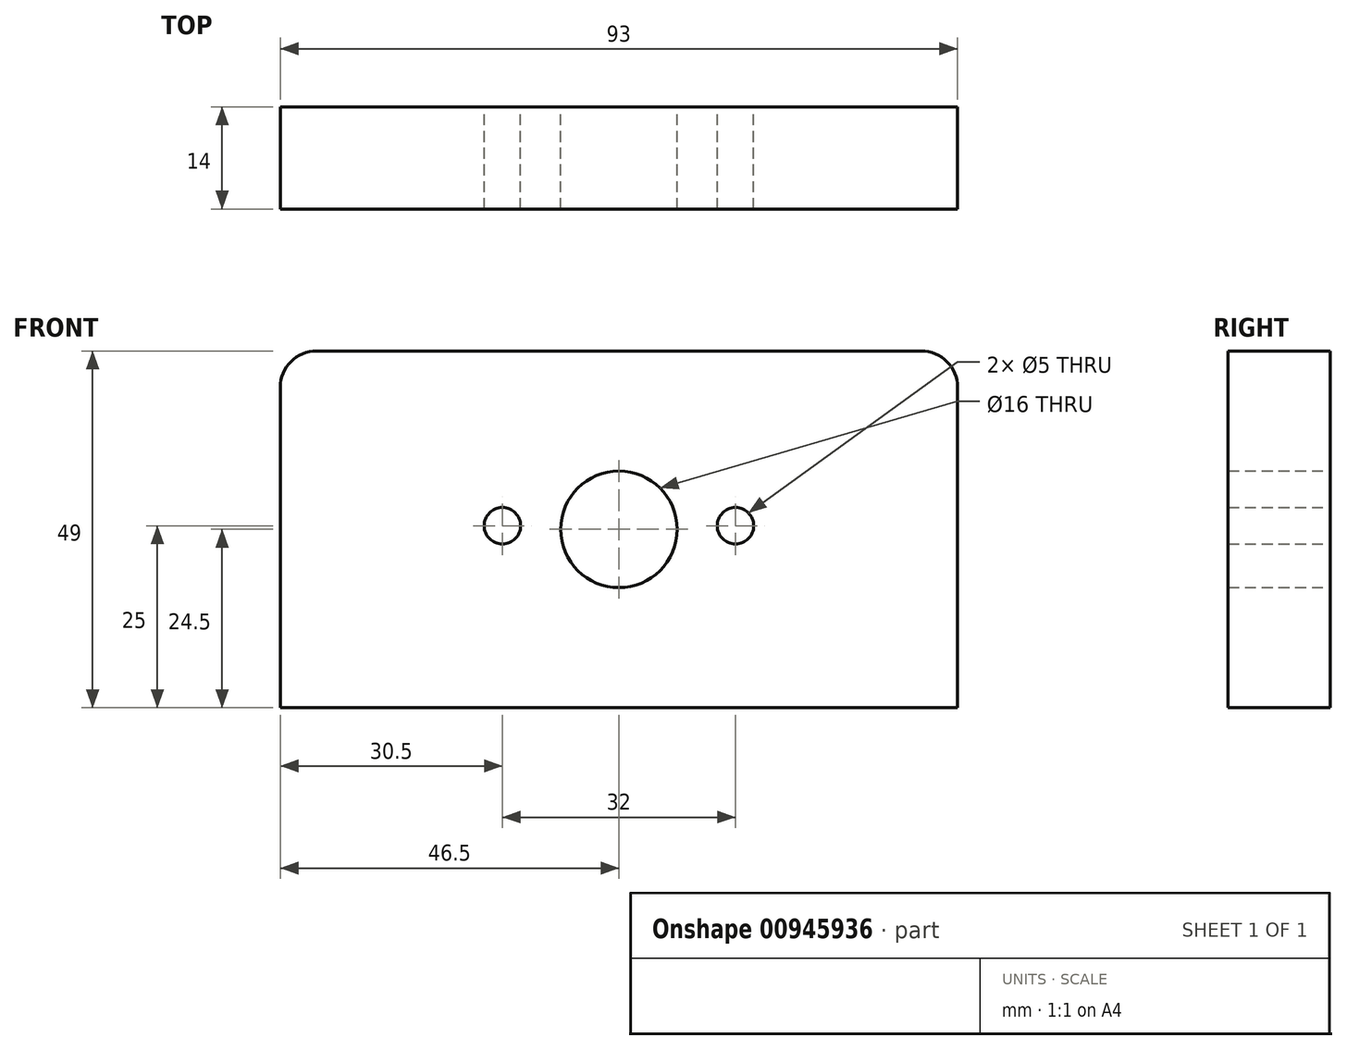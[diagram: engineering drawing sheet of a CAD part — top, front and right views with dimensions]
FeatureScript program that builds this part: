
annotation { "Feature Type Name" : "Feature", "Feature Type Description" : "" }
export const myFeature = defineFeature(function(context is Context, id is Id, definition is map)
    precondition{}
    {
        {
            var Q0;
            Q0=qCreatedBy(makeId("Front.planeOp"),FACE);
            var sketch = newSketch(context, id + "F0", { "sketchPlane" : qUnion([Q0])});
            skLineSegment(sketch, "E0.bottom", {"start": v(46.5, -24.5) * mm, "end": v(-46.5, -24.5) * mm});
            skLineSegment(sketch, "E0.top", {"start": v(41.5, 24.5) * mm, "end": v(-41.5, 24.5) * mm});
            skLineSegment(sketch, "E0.left", {"start": v(46.5, -24.5) * mm, "end": v(46.5, 19.5) * mm});
            skLineSegment(sketch, "E0.right", {"start": v(-46.5, -24.5) * mm, "end": v(-46.5, 19.5) * mm});
            skPoint(sketch, "E0.middle", {"position": v(0, 0) * mm});
            skPoint(sketch, "E1.visualSharp", {"position": v(-46.5, 24.5) * mm});
            skArc(sketch, "E1.filletArc", {"start": v(-41.5, 24.5) * mm, "mid": v(-45.04, 23.04) * mm, "end": v(-46.5, 19.5) * mm});
            skPoint(sketch, "E2.visualSharp", {"position": v(46.5, 24.5) * mm});
            skArc(sketch, "E2.filletArc", {"start": v(46.5, 19.5) * mm, "mid": v(45.04, 23.04) * mm, "end": v(41.5, 24.5) * mm});
            skCircle(sketch, "E3", {"center": v(0, 0) * mm, "radius": 8 * mm});
            skCircle(sketch, "E4", {"center": v(-16, 0.5) * mm, "radius": 2.5 * mm});
            skLineSegment(sketch, "E5", {"start": v(0, 0) * mm, "end": v(0, 24.5) * mm, "construction": true});
            skCircle(sketch, "E6.MirrorC", {"center": v(16, 0.5) * mm, "radius": 2.5 * mm});
            skSolve(sketch);
        }
        {
            var Q0;
            Q0 = qSketchRegion(id + "F0", true);
            extrude(context, id + "F1", {"entities" : qUnion([Q0]), "depth" : 14 * mm, "offsetDistance" : 25 * mm});
        }
    });
